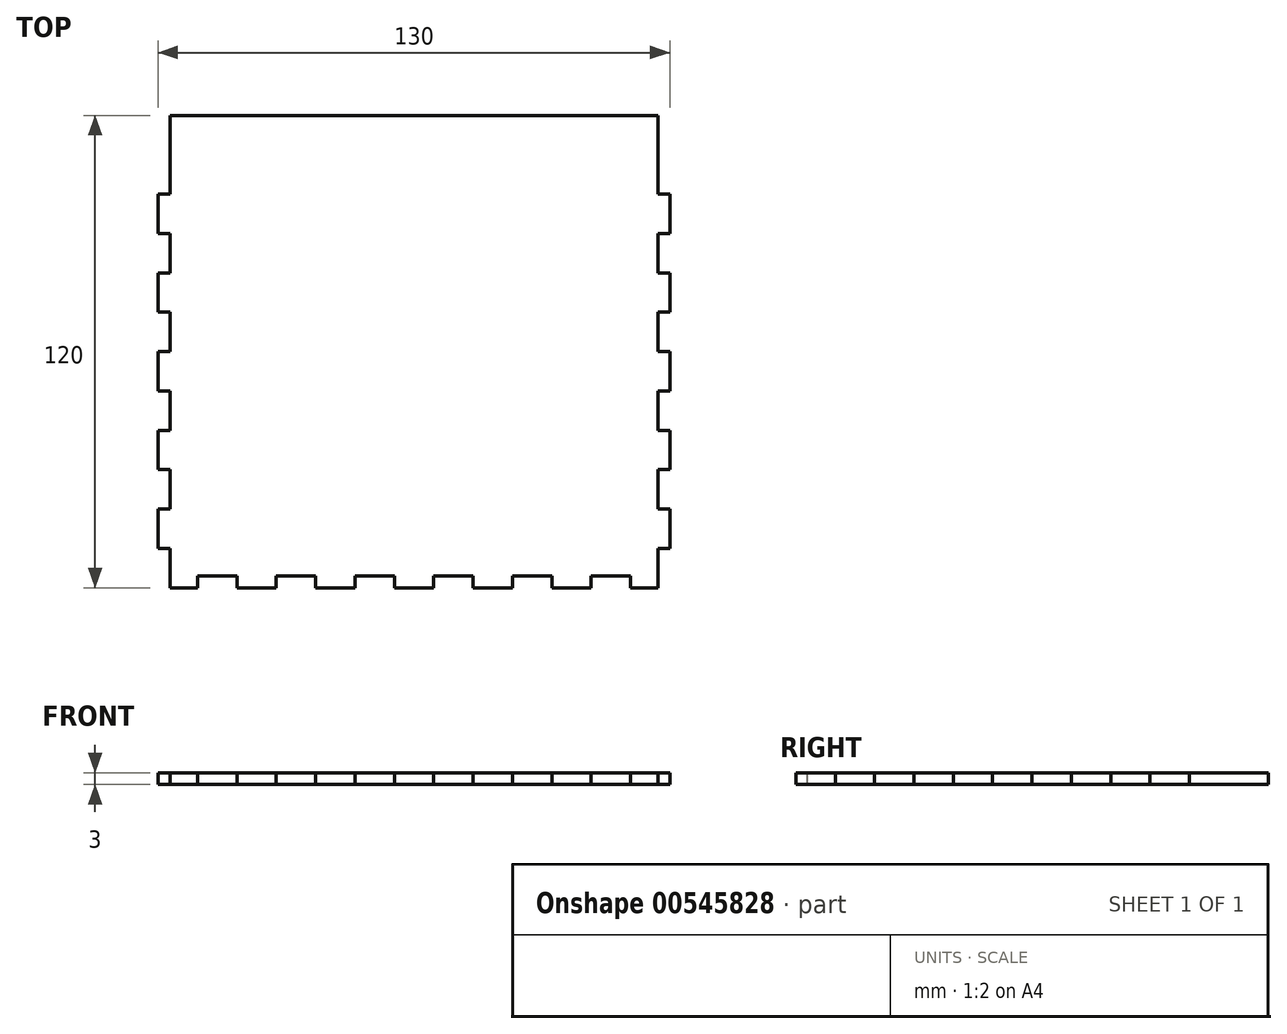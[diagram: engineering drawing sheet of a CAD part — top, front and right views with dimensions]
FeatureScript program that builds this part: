
annotation { "Feature Type Name" : "Feature", "Feature Type Description" : "" }
export const myFeature = defineFeature(function(context is Context, id is Id, definition is map)
    precondition{}
    {
        {
            var Q0;
            Q0=qCreatedBy(makeId("Top.planeOp"),FACE);
            var sketch = newSketch(context, id + "F0", { "sketchPlane" : qUnion([Q0])});
            skLineSegment(sketch, "E0.bottom", {"start": v(65, -60) * mm, "end": v(-65, -60) * mm});
            skLineSegment(sketch, "E0.top", {"start": v(65, 60) * mm, "end": v(-65, 60) * mm});
            skLineSegment(sketch, "E0.left", {"start": v(65, -60) * mm, "end": v(65, 60) * mm});
            skLineSegment(sketch, "E0.right", {"start": v(-65, -60) * mm, "end": v(-65, 60) * mm});
            skPoint(sketch, "E0.middle", {"position": v(0, 0) * mm});
            skSolve(sketch);
        }
        {
            var Q0;
            Q0=makeQuery(id+"F0.imprint","IMPRINT",FACE,{"disambiguationData":[TD([[makeQuery(id+"F0.imprint","IMPRINT",EDGE,{"derivedFrom":sQuery(id+"F0.wireOp",EDGE,"E0.bottom")}),-1.0]])]});
            var sketch = newSketch(context, id + "F1", { "sketchPlane" : qUnion([Q0])});
            skLineSegment(sketch, "E1.bottom", {"start": v(65, -60) * mm, "end": v(62, -60) * mm});
            skLineSegment(sketch, "E1.top", {"start": v(65, -50) * mm, "end": v(62, -50) * mm});
            skLineSegment(sketch, "E1.left", {"start": v(65, -60) * mm, "end": v(65, -50) * mm});
            skLineSegment(sketch, "E1.right", {"start": v(62, -60) * mm, "end": v(62, -50) * mm});
            skLineSegment(sketch, "E2.0.1.0", {"start": v(62, -40) * mm, "end": v(62, -30) * mm});
            skLineSegment(sketch, "E2.0.1.1", {"start": v(65, -40) * mm, "end": v(65, -30) * mm});
            skLineSegment(sketch, "E2.0.1.2", {"start": v(65, -30) * mm, "end": v(62, -30) * mm});
            skLineSegment(sketch, "E2.0.1.3", {"start": v(65, -40) * mm, "end": v(62, -40) * mm});
            skLineSegment(sketch, "E2.0.2.0", {"start": v(62, -20) * mm, "end": v(62, -10) * mm});
            skLineSegment(sketch, "E2.0.2.1", {"start": v(65, -20) * mm, "end": v(65, -10) * mm});
            skLineSegment(sketch, "E2.0.2.2", {"start": v(65, -10) * mm, "end": v(62, -10) * mm});
            skLineSegment(sketch, "E2.0.2.3", {"start": v(65, -20) * mm, "end": v(62, -20) * mm});
            skLineSegment(sketch, "E2.0.3.0", {"start": v(62, 0) * mm, "end": v(62, 10) * mm});
            skLineSegment(sketch, "E2.0.3.1", {"start": v(65, 0) * mm, "end": v(65, 10) * mm});
            skLineSegment(sketch, "E2.0.3.2", {"start": v(65, 10) * mm, "end": v(62, 10) * mm});
            skLineSegment(sketch, "E2.0.3.3", {"start": v(65, 0) * mm, "end": v(62, 0) * mm});
            skLineSegment(sketch, "E2.0.4.0", {"start": v(62, 20) * mm, "end": v(62, 30) * mm});
            skLineSegment(sketch, "E2.0.4.1", {"start": v(65, 20) * mm, "end": v(65, 30) * mm});
            skLineSegment(sketch, "E2.0.4.2", {"start": v(65, 30) * mm, "end": v(62, 30) * mm});
            skLineSegment(sketch, "E2.0.4.3", {"start": v(65, 20) * mm, "end": v(62, 20) * mm});
            skLineSegment(sketch, "E2.0.5.0", {"start": v(62, 40) * mm, "end": v(62, 50) * mm});
            skLineSegment(sketch, "E2.0.5.1", {"start": v(65, 40) * mm, "end": v(65, 50) * mm});
            skLineSegment(sketch, "E2.0.5.2", {"start": v(65, 50) * mm, "end": v(62, 50) * mm});
            skLineSegment(sketch, "E2.0.5.3", {"start": v(65, 40) * mm, "end": v(62, 40) * mm});
            skLineSegment(sketch, "E2.direction1", {"start": v(62, -60) * mm, "end": v(87, -60) * mm, "construction": true});
            skLineSegment(sketch, "E2.direction2", {"start": v(62, -60) * mm, "end": v(62, -40) * mm, "construction": true});
            skLineSegment(sketch, "E3", {"start": v(0, -56.46) * mm, "end": v(0, 57.33) * mm, "construction": true});
            skLineSegment(sketch, "E4.MirrorCS", {"start": v(-62, -60) * mm, "end": v(-62, -40) * mm, "construction": true});
            skLineSegment(sketch, "E5.MirrorCS", {"start": v(-62, -60) * mm, "end": v(-62, -50) * mm});
            skLineSegment(sketch, "E6.MirrorCS", {"start": v(-65, 20) * mm, "end": v(-65, 30) * mm});
            skLineSegment(sketch, "E7.MirrorCS", {"start": v(-62, 0) * mm, "end": v(-62, 10) * mm});
            skLineSegment(sketch, "E8.MirrorCS", {"start": v(-65, -20) * mm, "end": v(-62, -20) * mm});
            skLineSegment(sketch, "E9.MirrorCS", {"start": v(-65, -10) * mm, "end": v(-62, -10) * mm});
            skLineSegment(sketch, "E10.MirrorCS", {"start": v(-65, 20) * mm, "end": v(-62, 20) * mm});
            skLineSegment(sketch, "E11.MirrorCS", {"start": v(-65, -20) * mm, "end": v(-65, -10) * mm});
            skLineSegment(sketch, "E12.MirrorCS", {"start": v(-62, -20) * mm, "end": v(-62, -10) * mm});
            skLineSegment(sketch, "E13.MirrorCS", {"start": v(-65, 40) * mm, "end": v(-65, 50) * mm});
            skLineSegment(sketch, "E14.MirrorCS", {"start": v(-65, -40) * mm, "end": v(-62, -40) * mm});
            skLineSegment(sketch, "E15.MirrorCS", {"start": v(-65, 40) * mm, "end": v(-62, 40) * mm});
            skLineSegment(sketch, "E16.MirrorCS", {"start": v(-65, 50) * mm, "end": v(-62, 50) * mm});
            skLineSegment(sketch, "E17.MirrorCS", {"start": v(-62, 40) * mm, "end": v(-62, 50) * mm});
            skLineSegment(sketch, "E18.MirrorCS", {"start": v(-62, 20) * mm, "end": v(-62, 30) * mm});
            skLineSegment(sketch, "E19.MirrorCS", {"start": v(-65, 0) * mm, "end": v(-65, 10) * mm});
            skLineSegment(sketch, "E20.MirrorCS", {"start": v(-65, 10) * mm, "end": v(-62, 10) * mm});
            skLineSegment(sketch, "E21.MirrorCS", {"start": v(-65, 0) * mm, "end": v(-62, 0) * mm});
            skLineSegment(sketch, "E22.MirrorCS", {"start": v(-65, -60) * mm, "end": v(-62, -60) * mm});
            skLineSegment(sketch, "E23.MirrorCS", {"start": v(-65, -60) * mm, "end": v(-65, -50) * mm});
            skLineSegment(sketch, "E24.MirrorCS", {"start": v(-62, -40) * mm, "end": v(-62, -30) * mm});
            skLineSegment(sketch, "E25.MirrorCS", {"start": v(-65, -40) * mm, "end": v(-65, -30) * mm});
            skLineSegment(sketch, "E26.MirrorCS", {"start": v(-65, -30) * mm, "end": v(-62, -30) * mm});
            skLineSegment(sketch, "E27.MirrorCS", {"start": v(-65, 30) * mm, "end": v(-62, 30) * mm});
            skLineSegment(sketch, "E28.MirrorCS", {"start": v(-65, -50) * mm, "end": v(-62, -50) * mm});
            skSolve(sketch);
        }
        {
            var Q0;
            Q0=qSketchRegion(id+"F0",true);
            extrude(context, id + "F2", {"entities" : qUnion([Q0]), "depth" : 3 * mm, "offsetDistance" : 25 * mm});
        }
        {
            var Q0;
            Q0=qSketchRegion(id+"F1",true);
            extrude(context, id + "F3", {"entities" : qUnion([Q0]), "operationType" : NewBodyOperationType.REMOVE, "depth" : 25 * mm, "offsetDistance" : 25 * mm});
        }
        {
            var Q0;
            Q0=makeQuery(id+"F2.opExtrude","CAP_FACE",FACE,{"disambiguationData":[OSD([sQuery(id+"F0.wireOp",EDGE,"E0.bottom"),sQuery(id+"F0.wireOp",EDGE,"E0.top"),sQuery(id+"F0.wireOp",EDGE,"E0.left"),sQuery(id+"F0.wireOp",EDGE,"E0.right")])],"isStart":false});
            var sketch = newSketch(context, id + "F4", { "sketchPlane" : qUnion([Q0])});
            skPoint(sketch, "E29.firstSnap0", {"position": v(0, -60) * mm});
            skLineSegment(sketch, "E29.bottom", {"start": v(-55, -60) * mm, "end": v(-45, -60) * mm});
            skLineSegment(sketch, "E29.top", {"start": v(-55, -57) * mm, "end": v(-45, -57) * mm});
            skLineSegment(sketch, "E29.left", {"start": v(-55, -60) * mm, "end": v(-55, -57) * mm});
            skLineSegment(sketch, "E29.right", {"start": v(-45, -60) * mm, "end": v(-45, -57) * mm});
            skLineSegment(sketch, "E30.1.0.0", {"start": v(-35, -57) * mm, "end": v(-25, -57) * mm});
            skLineSegment(sketch, "E30.1.0.1", {"start": v(-35, -60) * mm, "end": v(-25, -60) * mm});
            skLineSegment(sketch, "E30.1.0.2", {"start": v(-25, -60) * mm, "end": v(-25, -57) * mm});
            skLineSegment(sketch, "E30.1.0.3", {"start": v(-35, -60) * mm, "end": v(-35, -57) * mm});
            skLineSegment(sketch, "E30.2.0.0", {"start": v(-15, -57) * mm, "end": v(-5, -57) * mm});
            skLineSegment(sketch, "E30.2.0.1", {"start": v(-15, -60) * mm, "end": v(-5, -60) * mm});
            skLineSegment(sketch, "E30.2.0.2", {"start": v(-5, -60) * mm, "end": v(-5, -57) * mm});
            skLineSegment(sketch, "E30.2.0.3", {"start": v(-15, -60) * mm, "end": v(-15, -57) * mm});
            skLineSegment(sketch, "E30.3.0.0", {"start": v(5, -57) * mm, "end": v(15, -57) * mm});
            skLineSegment(sketch, "E30.3.0.1", {"start": v(5, -60) * mm, "end": v(15, -60) * mm});
            skLineSegment(sketch, "E30.3.0.2", {"start": v(15, -60) * mm, "end": v(15, -57) * mm});
            skLineSegment(sketch, "E30.3.0.3", {"start": v(5, -60) * mm, "end": v(5, -57) * mm});
            skLineSegment(sketch, "E30.4.0.0", {"start": v(25, -57) * mm, "end": v(35, -57) * mm});
            skLineSegment(sketch, "E30.4.0.1", {"start": v(25, -60) * mm, "end": v(35, -60) * mm});
            skLineSegment(sketch, "E30.4.0.2", {"start": v(35, -60) * mm, "end": v(35, -57) * mm});
            skLineSegment(sketch, "E30.4.0.3", {"start": v(25, -60) * mm, "end": v(25, -57) * mm});
            skLineSegment(sketch, "E30.5.0.0", {"start": v(45, -57) * mm, "end": v(55, -57) * mm});
            skLineSegment(sketch, "E30.5.0.1", {"start": v(45, -60) * mm, "end": v(55, -60) * mm});
            skLineSegment(sketch, "E30.5.0.2", {"start": v(55, -60) * mm, "end": v(55, -57) * mm});
            skLineSegment(sketch, "E30.5.0.3", {"start": v(45, -60) * mm, "end": v(45, -57) * mm});
            skLineSegment(sketch, "E30.direction1", {"start": v(-55, -57) * mm, "end": v(-35, -57) * mm, "construction": true});
            skSolve(sketch);
        }
        {
            var Q0;
            Q0=qSketchRegion(id+"F4",true);
            extrude(context, id + "F5", {"entities" : qUnion([Q0]), "operationType" : NewBodyOperationType.REMOVE, "oppositeDirection" : true, "depth" : 25 * mm, "offsetDistance" : 25 * mm});
        }
        {
            var Q0;
            Q0=makeQuery(id+"F2.opExtrude","CAP_FACE",FACE,{"disambiguationData":[OSD([sQuery(id+"F0.wireOp",EDGE,"E0.bottom"),sQuery(id+"F0.wireOp",EDGE,"E0.top"),sQuery(id+"F0.wireOp",EDGE,"E0.left"),sQuery(id+"F0.wireOp",EDGE,"E0.right")])],"isStart":false});
            var sketch = newSketch(context, id + "F6", { "sketchPlane" : qUnion([Q0])});
            skLineSegment(sketch, "E31.bottom", {"start": v(65, 50) * mm, "end": v(62, 50) * mm});
            skLineSegment(sketch, "E31.top", {"start": v(65, 60) * mm, "end": v(62, 60) * mm});
            skLineSegment(sketch, "E31.left", {"start": v(65, 50) * mm, "end": v(65, 60) * mm});
            skLineSegment(sketch, "E31.right", {"start": v(62, 50) * mm, "end": v(62, 60) * mm});
            skLineSegment(sketch, "E32.bottom", {"start": v(-65, 50) * mm, "end": v(-62, 50) * mm});
            skLineSegment(sketch, "E32.top", {"start": v(-65, 60) * mm, "end": v(-62, 60) * mm});
            skLineSegment(sketch, "E32.left", {"start": v(-65, 50) * mm, "end": v(-65, 60) * mm});
            skLineSegment(sketch, "E32.right", {"start": v(-62, 50) * mm, "end": v(-62, 60) * mm});
            skSolve(sketch);
        }
        {
            var Q0;
            Q0 = qSketchRegion(id + "F6", true);
            extrude(context, id + "F7", {"entities" : qUnion([Q0]), "operationType" : NewBodyOperationType.REMOVE, "oppositeDirection" : true, "depth" : 25 * mm, "offsetDistance" : 25 * mm});
        }
    });
